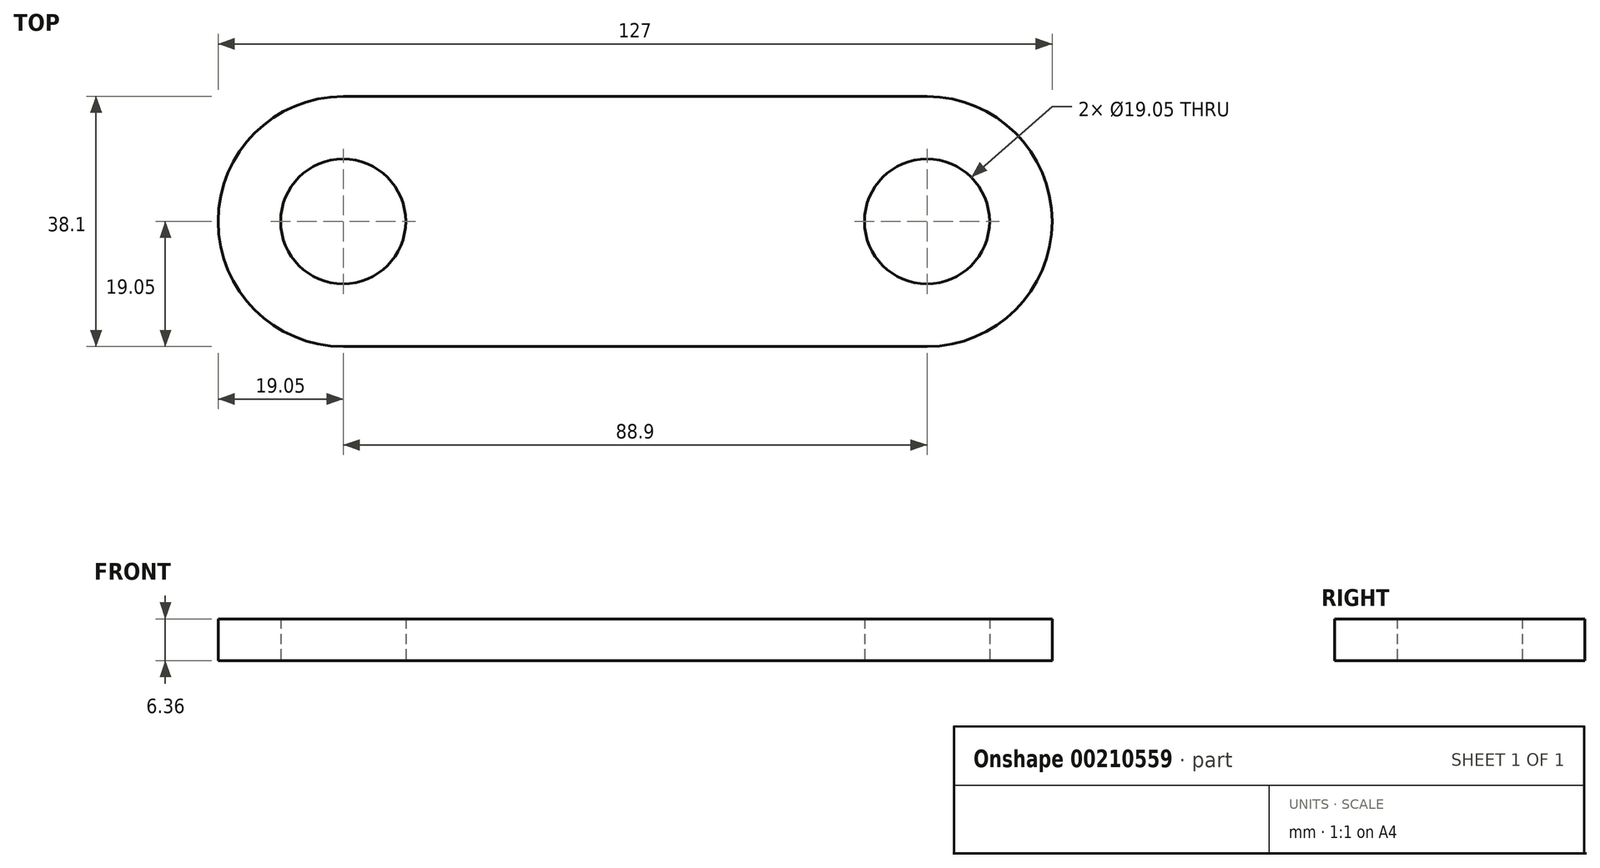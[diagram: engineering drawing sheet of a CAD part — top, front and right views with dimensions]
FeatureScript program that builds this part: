
annotation { "Feature Type Name" : "Feature", "Feature Type Description" : "" }
export const myFeature = defineFeature(function(context is Context, id is Id, definition is map)
    precondition{}
    {
        {
            var Q0;
            Q0=qCreatedBy(makeId("Top.planeOp"),FACE);
            var sketch = newSketch(context, id + "F0", { "sketchPlane" : qUnion([Q0])});
            skLineSegment(sketch, "E0.bottom", {"start": v(-44.45, 19.05) * mm, "end": v(44.45, 19.05) * mm});
            skLineSegment(sketch, "E0.top", {"start": v(-44.45, -19.05) * mm, "end": v(44.45, -19.05) * mm});
            skArc(sketch, "E1", {"start": v(-44.45, 19.05) * mm, "mid": v(-63.5, 0) * mm, "end": v(-44.45, -19.05) * mm});
            skArc(sketch, "E2", {"start": v(44.45, -19.05) * mm, "mid": v(63.5, 0) * mm, "end": v(44.45, 19.05) * mm});
            skCircle(sketch, "E3", {"center": v(44.45, 0) * mm, "radius": 9.53 * mm});
            skCircle(sketch, "E4", {"center": v(-44.45, 0) * mm, "radius": 9.53 * mm});
            skSolve(sketch);
        }
        {
            var Q0;
            Q0 = qSketchRegion(id + "F0", true);
            extrude(context, id + "F1", {"entities" : qUnion([Q0]), "endBound" : BoundingType.SYMMETRIC, "depth" : 6.35 * mm});
        }
    });
